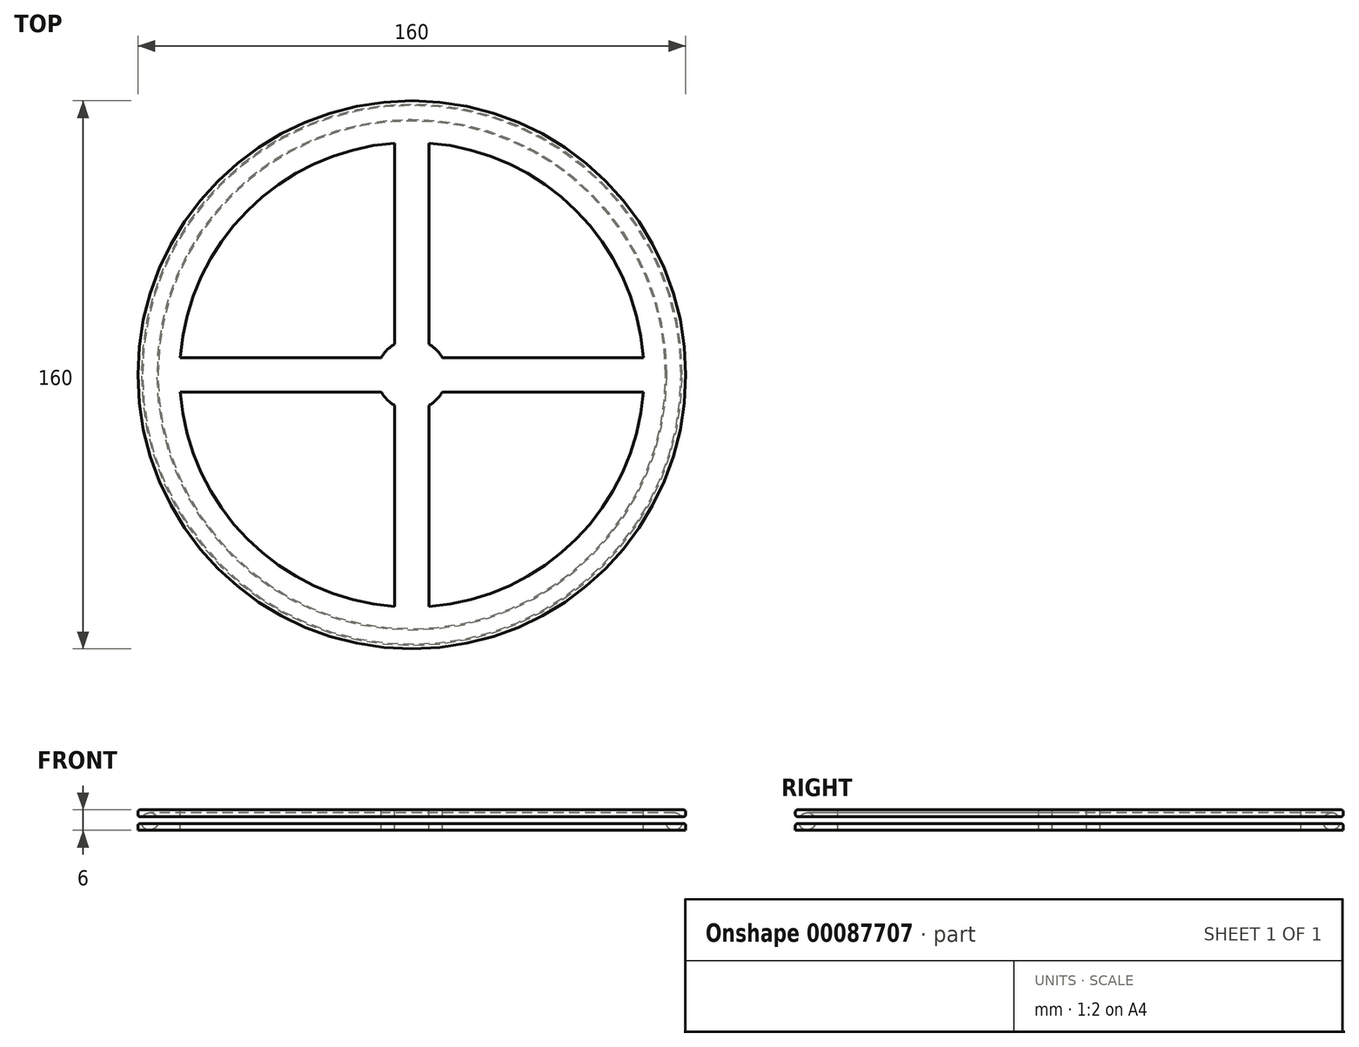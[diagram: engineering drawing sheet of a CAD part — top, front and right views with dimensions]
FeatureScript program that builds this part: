
annotation { "Feature Type Name" : "Feature", "Feature Type Description" : "" }
export const myFeature = defineFeature(function(context is Context, id is Id, definition is map)
    precondition{}
    {
        {
            var Q0;
            Q0=qCreatedBy(makeId("Front.planeOp"),FACE);
            var sketch = newSketch(context, id + "F0", { "sketchPlane" : qUnion([Q0])});
            skLineSegment(sketch, "E0.bottom", {"start": v(-29.31, 3) * mm, "end": v(-28.97, 3) * mm});
            skLineSegment(sketch, "E0.top", {"start": v(-30, 1) * mm, "end": v(50, 1) * mm});
            skLineSegment(sketch, "E1", {"start": v(-29.31, 5) * mm, "end": v(-28.63, 5) * mm});
            skLineSegment(sketch, "E2", {"start": v(-30, 5.69) * mm, "end": v(-30, 6.31) * mm});
            skLineSegment(sketch, "E3", {"start": v(-29.31, 7) * mm, "end": v(50, 7) * mm});
            skLineSegment(sketch, "E4", {"start": v(-30, 2.31) * mm, "end": v(-30, 1) * mm});
            skArc(sketch, "E5.filletArc", {"start": v(-29.31, 3) * mm, "mid": v(-29.8, 2.8) * mm, "end": v(-30, 2.31) * mm});
            skArc(sketch, "E6.filletArc", {"start": v(-30, 5.69) * mm, "mid": v(-29.8, 5.2) * mm, "end": v(-29.31, 5) * mm});
            skPoint(sketch, "E7.visualSharp", {"position": v(-30, 7) * mm});
            skArc(sketch, "E7.filletArc", {"start": v(-29.31, 7) * mm, "mid": v(-29.8, 6.8) * mm, "end": v(-30, 6.31) * mm});
            skLineSegment(sketch, "E8", {"start": v(-24.13, 3) * mm, "end": v(0, 3) * mm});
            skLineSegment(sketch, "E9", {"start": v(-24.46, 5) * mm, "end": v(50, 5) * mm});
            skArc(sketch, "E10", {"start": v(-24.46, 5) * mm, "mid": v(-26.56, 6.12) * mm, "end": v(-28.64, 4.99) * mm});
            skArc(sketch, "E11", {"start": v(-28.97, 3) * mm, "mid": v(-26.55, 1.12) * mm, "end": v(-24.13, 3) * mm});
            skLineSegment(sketch, "E12", {"start": v(0, 3) * mm, "end": v(50, 3) * mm});
            skLineSegment(sketch, "E13", {"start": v(50, 11.7) * mm, "end": v(50, 7) * mm});
            skLineSegment(sketch, "E14", {"start": v(50, 3) * mm, "end": v(50, 1) * mm});
            skPoint(sketch, "E15.end.orphan", {"position": v(0, 5) * mm});
            skPoint(sketch, "E15.start.orphan", {"position": v(0, 7) * mm});
            skLineSegment(sketch, "E16", {"start": v(50, 7) * mm, "end": v(50, 5) * mm});
            skSolve(sketch);
        }
        {
            var Q0;
            Q0=makeQuery(id+"F0.imprint","IMPRINT",FACE,{"disambiguationData":[TD([[makeQuery(id+"F0.imprint","IMPRINT",EDGE,{"derivedFrom":sQuery(id+"F0.wireOp",EDGE,"E0.bottom")}),-1.0]])]});
            var Q1;
            {var subQ1=sQuery(id+"F0.wireOp",EDGE,"E1");Q1=makeQuery(id+"F0.imprint","IMPRINT",FACE,{"disambiguationData":[TD([[makeQuery(id+"F0.imprint","IMPRINT",EDGE,{"derivedFrom":subQ1}),1.0]])]});}
            var Q2;
            Q2=sQuery(id+"F0.wireOp",EDGE,"E14");
            revolve(context, id + "F1", {"entities" : qUnion([Q0, Q1]), "axis" : qUnion([Q2]), "revolveType" : RevolveType.FULL});
        }
        {
            var Q0;
            Q0=makeQuery(id+"F1.opRevolve","SWEPT_FACE",FACE,{"disambiguationData":[OSD([sQuery(id+"F0.wireOp",EDGE,"E3")])]});
            var sketch = newSketch(context, id + "F2", { "sketchPlane" : qUnion([Q0])});
            skCircle(sketch, "E17.0", {"center": v(50, 0) * mm, "radius": 79.31 * mm});
            skLineSegment(sketch, "E18", {"start": v(50, 0) * mm, "end": v(129.31, 0) * mm, "construction": true});
            skLineSegment(sketch, "E19", {"start": v(50, 0) * mm, "end": v(-29.31, 0) * mm, "construction": true});
            skLineSegment(sketch, "E20", {"start": v(50, 79.31) * mm, "end": v(50, -67.83) * mm, "construction": true});
            skLineSegment(sketch, "E21", {"start": v(-6.08, 56.08) * mm, "end": v(50, 0) * mm});
            skLineSegment(sketch, "E22", {"start": v(50, 0) * mm, "end": v(106.08, -56.08) * mm});
            skLineSegment(sketch, "E23", {"start": v(50, 0) * mm, "end": v(106.08, 56.08) * mm});
            skLineSegment(sketch, "E24", {"start": v(50, 0) * mm, "end": v(-6.08, -56.08) * mm});
            skCircle(sketch, "E25", {"center": v(50, 0) * mm, "radius": 10.24 * mm});
            skLineSegment(sketch, "E26", {"start": v(55.85, -79.1) * mm, "end": v(44.15, 79.1) * mm});
            skLineSegment(sketch, "E27", {"start": v(50, 0) * mm, "end": v(129.1, 5.85) * mm});
            skLineSegment(sketch, "E28", {"start": v(50, 0) * mm, "end": v(-29.1, -5.85) * mm});
            skLineSegment(sketch, "E29", {"start": v(44.15, -79.1) * mm, "end": v(55.85, 79.1) * mm});
            skLineSegment(sketch, "E30", {"start": v(50, 0) * mm, "end": v(-29.1, 5.85) * mm});
            skLineSegment(sketch, "E31", {"start": v(50, 0) * mm, "end": v(129.1, -5.85) * mm});
            skArc(sketch, "E32", {"start": v(45, 67.65) * mm, "mid": v(21.75, 61.67) * mm, "end": v(2.04, 47.96) * mm});
            skArc(sketch, "E33", {"start": v(50, 67.83) * mm, "mid": v(47.5, 67.78) * mm, "end": v(45, 67.65) * mm});
            skArc(sketch, "E34", {"start": v(55, 67.65) * mm, "mid": v(52.5, 67.78) * mm, "end": v(50, 67.83) * mm});
            skArc(sketch, "E35", {"start": v(97.96, 47.96) * mm, "mid": v(78.25, 61.67) * mm, "end": v(55, 67.65) * mm});
            skArc(sketch, "E36", {"start": v(117.65, 5) * mm, "mid": v(111.67, 28.25) * mm, "end": v(97.96, 47.96) * mm});
            skArc(sketch, "E37", {"start": v(117.83, 0) * mm, "mid": v(117.78, 2.5) * mm, "end": v(117.65, 5) * mm});
            skArc(sketch, "E38", {"start": v(117.65, -5) * mm, "mid": v(117.78, -2.5) * mm, "end": v(117.83, 0) * mm});
            skArc(sketch, "E39", {"start": v(97.96, -47.96) * mm, "mid": v(111.67, -28.25) * mm, "end": v(117.65, -5) * mm});
            skArc(sketch, "E40", {"start": v(55, -67.65) * mm, "mid": v(78.25, -61.67) * mm, "end": v(97.96, -47.96) * mm});
            skLineSegment(sketch, "E41", {"start": v(50, -67.83) * mm, "end": v(50, -79.31) * mm, "construction": true});
            skArc(sketch, "E42", {"start": v(50, -67.83) * mm, "mid": v(52.5, -67.78) * mm, "end": v(55, -67.65) * mm});
            skArc(sketch, "E43", {"start": v(45, -67.65) * mm, "mid": v(47.5, -67.78) * mm, "end": v(50, -67.83) * mm});
            skArc(sketch, "E44", {"start": v(2.04, -47.96) * mm, "mid": v(21.75, -61.67) * mm, "end": v(45, -67.65) * mm});
            skArc(sketch, "E45", {"start": v(-17.65, -5) * mm, "mid": v(-11.67, -28.25) * mm, "end": v(2.04, -47.96) * mm});
            skArc(sketch, "E46", {"start": v(-17.83, 0) * mm, "mid": v(-17.78, -2.5) * mm, "end": v(-17.65, -5) * mm});
            skArc(sketch, "E47", {"start": v(-17.65, 5) * mm, "mid": v(-17.78, 2.5) * mm, "end": v(-17.83, 0) * mm});
            skArc(sketch, "E48", {"start": v(2.04, 47.96) * mm, "mid": v(-11.67, 28.25) * mm, "end": v(-17.65, 5) * mm});
            skPoint(sketch, "E49", {"position": v(21.75, 61.67) * mm});
            skPoint(sketch, "E50", {"position": v(47.5, 67.78) * mm});
            skPoint(sketch, "E51", {"position": v(52.5, 67.78) * mm});
            skPoint(sketch, "E52", {"position": v(78.25, 61.67) * mm});
            skPoint(sketch, "E53", {"position": v(111.67, 28.25) * mm});
            skPoint(sketch, "E54", {"position": v(117.78, 2.5) * mm});
            skPoint(sketch, "E55", {"position": v(117.78, -2.5) * mm});
            skPoint(sketch, "E56", {"position": v(111.67, -28.25) * mm});
            skPoint(sketch, "E57", {"position": v(78.25, -61.67) * mm});
            skPoint(sketch, "E58", {"position": v(52.5, -67.78) * mm});
            skPoint(sketch, "E59", {"position": v(47.5, -67.78) * mm});
            skPoint(sketch, "E60", {"position": v(21.75, -61.67) * mm});
            skPoint(sketch, "E61", {"position": v(-11.67, -28.25) * mm});
            skPoint(sketch, "E62", {"position": v(-17.78, -2.5) * mm});
            skPoint(sketch, "E63", {"position": v(-17.78, 2.5) * mm});
            skPoint(sketch, "E64", {"position": v(-11.67, 28.25) * mm});
            skLineSegment(sketch, "E65", {"start": v(45, 67.65) * mm, "end": v(45, -67.65) * mm});
            skLineSegment(sketch, "E66", {"start": v(55, -67.65) * mm, "end": v(55, 67.65) * mm});
            skLineSegment(sketch, "E67", {"start": v(-17.65, -5) * mm, "end": v(117.65, -5) * mm});
            skLineSegment(sketch, "E68", {"start": v(-17.65, 5) * mm, "end": v(117.65, 5) * mm});
            skSolve(sketch);
        }
        {
            var Q0;
            {var subQ0=sQuery(id+"F2.wireOp",EDGE,"E36");Q0=makeQuery(id+"F2.imprint","IMPRINT",FACE,{"disambiguationData":[TD([[makeQuery(id+"F2.imprint","IMPRINT",EDGE,{"derivedFrom":subQ0}),1.0]])]});}
            var Q1;
            {var subQ0=sQuery(id+"F2.wireOp",EDGE,"E35");Q1=makeQuery(id+"F2.imprint","IMPRINT",FACE,{"disambiguationData":[TD([[makeQuery(id+"F2.imprint","IMPRINT",EDGE,{"derivedFrom":subQ0}),1.0]])]});}
            var Q2;
            {var subQ0=sQuery(id+"F2.wireOp",EDGE,"E32");Q2=makeQuery(id+"F2.imprint","IMPRINT",FACE,{"disambiguationData":[TD([[makeQuery(id+"F2.imprint","IMPRINT",EDGE,{"derivedFrom":subQ0}),1.0]])]});}
            var Q3;
            {var subQ0=sQuery(id+"F2.wireOp",EDGE,"E48");Q3=makeQuery(id+"F2.imprint","IMPRINT",FACE,{"disambiguationData":[TD([[makeQuery(id+"F2.imprint","IMPRINT",EDGE,{"derivedFrom":subQ0}),1.0]])]});}
            var Q4;
            {var subQ0=sQuery(id+"F2.wireOp",EDGE,"E45");Q4=makeQuery(id+"F2.imprint","IMPRINT",FACE,{"disambiguationData":[TD([[makeQuery(id+"F2.imprint","IMPRINT",EDGE,{"derivedFrom":subQ0}),1.0]])]});}
            var Q5;
            {var subQ0=sQuery(id+"F2.wireOp",EDGE,"E44");Q5=makeQuery(id+"F2.imprint","IMPRINT",FACE,{"disambiguationData":[TD([[makeQuery(id+"F2.imprint","IMPRINT",EDGE,{"derivedFrom":subQ0}),1.0]])]});}
            var Q6;
            {var subQ0=sQuery(id+"F2.wireOp",EDGE,"E40");Q6=makeQuery(id+"F2.imprint","IMPRINT",FACE,{"disambiguationData":[TD([[makeQuery(id+"F2.imprint","IMPRINT",EDGE,{"derivedFrom":subQ0}),1.0]])]});}
            var Q7;
            {var subQ0=sQuery(id+"F2.wireOp",EDGE,"E39");Q7=makeQuery(id+"F2.imprint","IMPRINT",FACE,{"disambiguationData":[TD([[makeQuery(id+"F2.imprint","IMPRINT",EDGE,{"derivedFrom":subQ0}),1.0]])]});}
            extrude(context, id + "F3", {"entities" : qUnion([Q0, Q1, Q2, Q3, Q4, Q5, Q6, Q7]), "operationType" : NewBodyOperationType.REMOVE, "endBound" : BoundingType.THROUGH_ALL, "oppositeDirection" : true, "depth" : 11.2 * mm});
        }
    });
